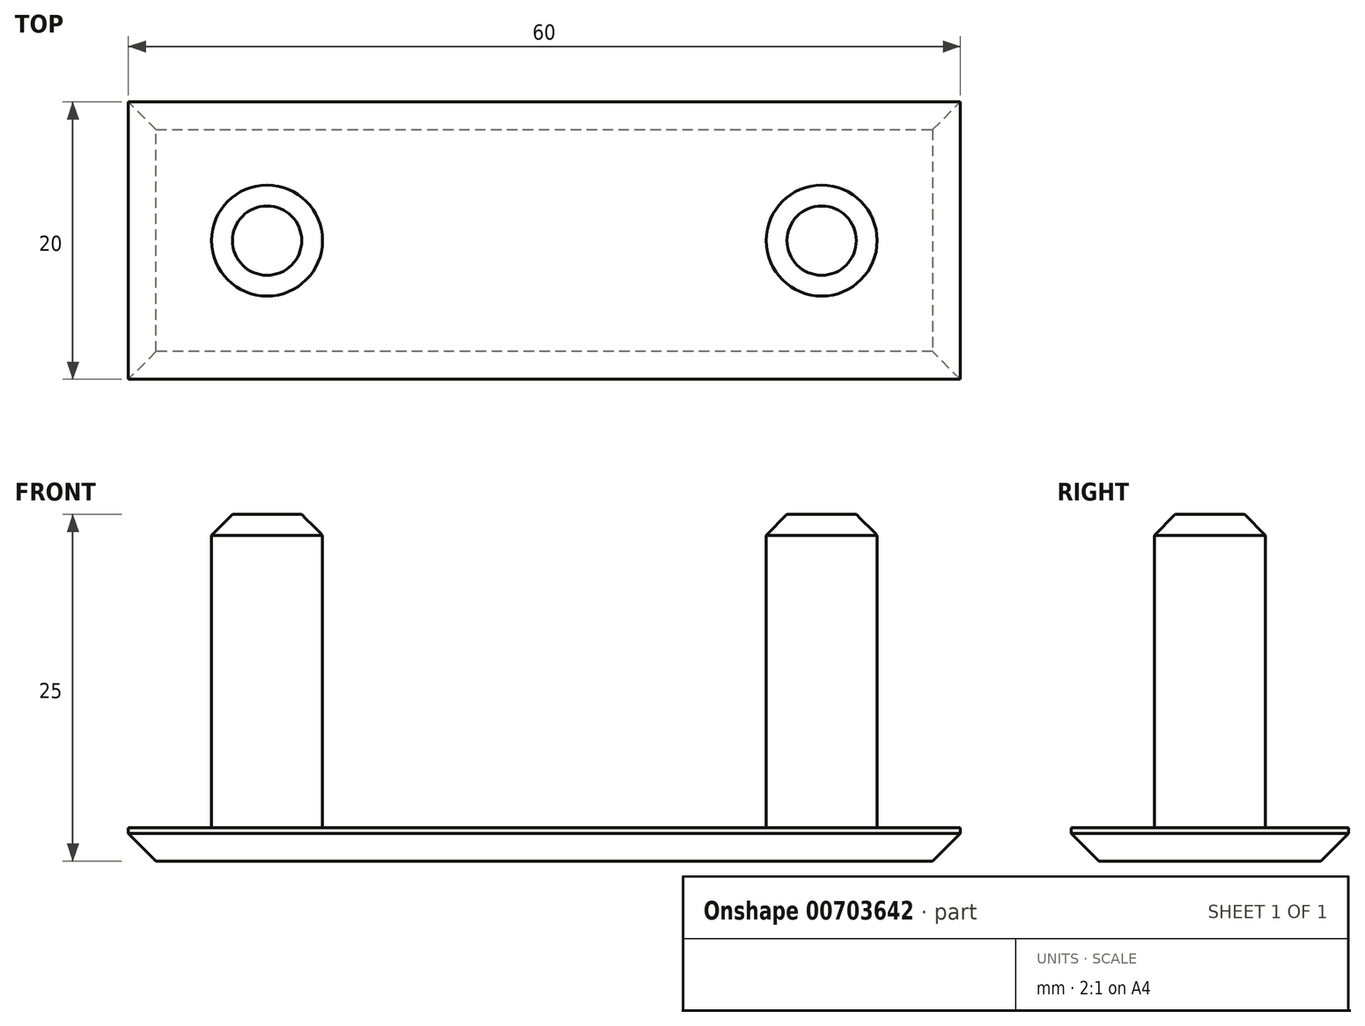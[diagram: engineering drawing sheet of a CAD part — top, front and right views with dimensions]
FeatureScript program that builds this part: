
annotation { "Feature Type Name" : "Feature", "Feature Type Description" : "" }
export const myFeature = defineFeature(function(context is Context, id is Id, definition is map)
    precondition{}
    {
        {
            var Q0;
            Q0=qCreatedBy(makeId("Top.planeOp"),FACE);
            var sketch = newSketch(context, id + "F0", { "sketchPlane" : qUnion([Q0])});
            skLineSegment(sketch, "E0.bottom", {"start": v(30, -10) * mm, "end": v(-30, -10) * mm});
            skLineSegment(sketch, "E0.top", {"start": v(30, 10) * mm, "end": v(-30, 10) * mm});
            skLineSegment(sketch, "E0.left", {"start": v(30, -10) * mm, "end": v(30, 10) * mm});
            skLineSegment(sketch, "E0.right", {"start": v(-30, -10) * mm, "end": v(-30, 10) * mm});
            skPoint(sketch, "E0.middle", {"position": v(0, 0) * mm});
            skCircle(sketch, "E1", {"center": v(-20, 0) * mm, "radius": 4 * mm});
            skCircle(sketch, "E2", {"center": v(20, 0) * mm, "radius": 4 * mm});
            skLineSegment(sketch, "E3", {"start": v(-20, 0) * mm, "end": v(20, 0) * mm});
            skSolve(sketch);
        }
        {
            var Q0;
            Q0=makeQuery(id+"F0.imprint","IMPRINT",FACE,{"disambiguationData":[TD([[makeQuery(id+"F0.imprint","IMPRINT",EDGE,{"derivedFrom":sQuery(id+"F0.wireOp",EDGE,"E0.bottom")}),-1.0]])]});
            var Q1;
            Q1=makeQuery(id+"F0.imprint","IMPRINT",FACE,{"disambiguationData":[TD([[makeQuery(id+"F0.imprint","IMPRINT",EDGE,{"derivedFrom":sQuery(id+"F0.wireOp",EDGE,"E1")}),1.0]])]});
            var Q2;
            Q2=makeQuery(id+"F0.imprint","IMPRINT",FACE,{"disambiguationData":[TD([[makeQuery(id+"F0.imprint","IMPRINT",EDGE,{"derivedFrom":sQuery(id+"F0.wireOp",EDGE,"E2")}),1.0]])]});
            extrude(context, id + "F1", {"entities" : qUnion([Q0, Q1, Q2]), "depth" : 2.4 * mm, "offsetDistance" : 25 * mm});
        }
        {
            var Q0;
            Q0=makeQuery(id+"F0.imprint","IMPRINT",FACE,{"disambiguationData":[TD([[makeQuery(id+"F0.imprint","IMPRINT",EDGE,{"derivedFrom":sQuery(id+"F0.wireOp",EDGE,"E1")}),1.0]])]});
            var Q1;
            Q1=makeQuery(id+"F0.imprint","IMPRINT",FACE,{"disambiguationData":[TD([[makeQuery(id+"F0.imprint","IMPRINT",EDGE,{"derivedFrom":sQuery(id+"F0.wireOp",EDGE,"E2")}),1.0]])]});
            extrude(context, id + "F2", {"entities" : qUnion([Q0, Q1]), "operationType" : NewBodyOperationType.ADD, "depth" : 25 * mm, "offsetDistance" : 25 * mm});
        }
        {
            var Q0;
            Q0=makeQuery(id+"F1.opExtrude","CAP_FACE",FACE,{"disambiguationData":[OSD([sQuery(id+"F0.wireOp",EDGE,"E0.bottom"),sQuery(id+"F0.wireOp",EDGE,"E0.top"),sQuery(id+"F0.wireOp",EDGE,"E0.left"),sQuery(id+"F0.wireOp",EDGE,"E0.right")])],"isStart":true});
            chamfer(context, id + "F3", {"entities" : qUnion([Q0]), "width" : 2 * mm, "tangentPropagation" : true});
        }
        {
            var Q0;
            Q0=makeQuery(id+"F2.opExtrude","CAP_EDGE",EDGE,{"disambiguationData":[OSD([sQuery(id+"F0.wireOp",EDGE,"E1")])],"isStart":false});
            var Q1;
            Q1=makeQuery(id+"F2.opExtrude","CAP_EDGE",EDGE,{"disambiguationData":[OSD([sQuery(id+"F0.wireOp",EDGE,"E2")])],"isStart":false});
            chamfer(context, id + "F4", {"entities" : qUnion([Q0, Q1]), "width" : 1.5 * mm, "tangentPropagation" : true});
        }
    });
